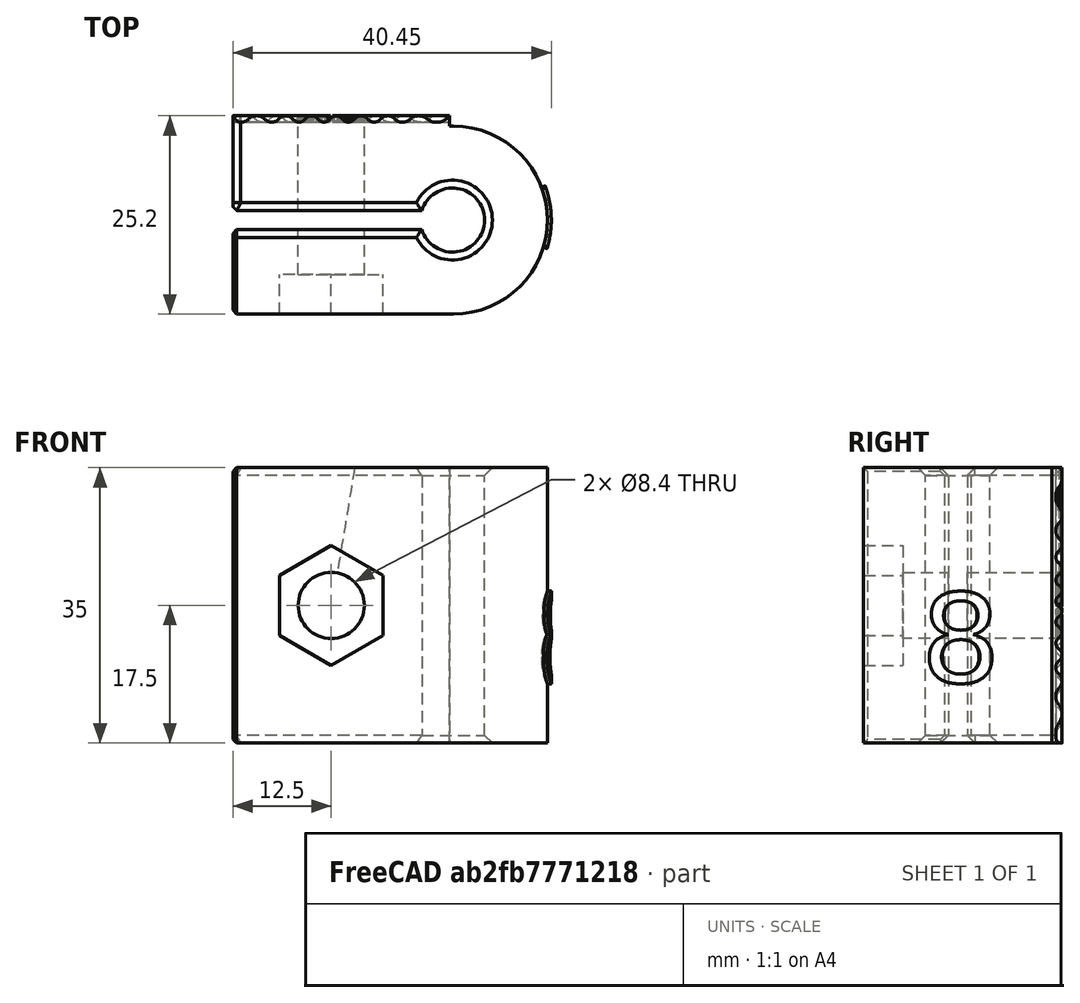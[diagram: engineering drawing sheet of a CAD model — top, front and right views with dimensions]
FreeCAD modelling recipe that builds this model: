
FCSTD DOCUMENT  (FreeCAD 1.1R43012 (Git))
Label: Rod clamp
License: All rights reserved
LicenseURL: https://en.wikipedia.org/wiki/All_rights_reserved
objects: Part::FeaturePython×3, Sketcher::SketchObject×3, App::Point×2, PartDesign::Body×2, Spreadsheet::Sheet×1, Part::RuledSurface×1, Part::Extrusion×1, Part::Box×1, Part::MultiCommon×1, Part::Part2DObjectPython×1, Part::Cylinder×1, PartDesign::Pad×1, PartDesign::FeatureBase×1, Mesh::Feature×1, PartDesign::Pocket×1, Part::MultiFuse×1, Part::Cut×1, Part::Chamfer×1
note: 28 computed .brp shape members not serialized (recipe doc carries the construction recipe); baked Part::Feature solids carry a one-line shape summary decoded from their .brp

FEATURE [Spreadsheet::Sheet] Spreadsheet  label="Parameters"
  cells = A1='Description of parameter; B1='Measurement; A2='Bolt diameter (mm); B2(bolt)=8; A3='Bolt diameter tolerance (mm); B3(BoltTolerance)=0.4; A4='Rod diameter (mm); B4(rod)=8; A5='Rod diameter tolerance (mm); B5(RodTolerance)=0.15; A7='Interface parameters; A8='Inner radius; B8(InnerRadius)=2; A9='Outer radius; B9(OuterRadius)=25; A10='Amplitude of waves; B10(amplitude)=0.8; A11='Number of waves; B11(NumberOfWaves)=36; A12='Interval (do not change); B12(Interval)=0.01
FEATURE [Part::FeaturePython] ParametricCurve  # WARN: FeaturePython — macro-defined, semantics opaque (R4)
  AttacherType = Attacher::AttachEngine3D
  Closed = false
  Continuity = C2
  EditFormulas = false
  F_X = 0
  F_Y = 0
  F_Z = 0
  F_a = 25
  F_b = 36
  F_c = 0.8
  F_d = [0,0]
  FormulaName = formula1
  Formulas = 0
  Interval = 0.01
  MakeFace = false
  PlusOneIteration = true
  Points = (630) [(25,0,0.4),(24.9988,0.249996,0.602621),(24.995,0.499967,0.738292),(24.9888,0.749888,0.791969),(24.98,0.999733,0.799956),(24.9688,1.24948,0.799593),+624 more]
  ShapeType = 0
  Sorted = false
  UpdateSpreadsheet = false
  UseSpreadsheet = false
  Version = 2023.05.06
  X = a*cos(t)
  Y = a*sin(t)
  Z = c * ( 3*((1 + sin(b*t))/2)^2 - 2*((1 + sin(b*t))/2)^3 )
  a = 25
  b = 36
  c = 0.8
  t_max = 6.28319
  t_min = 0
  expr: Interval = .Spreadsheet.Interval
  expr: a = .Spreadsheet.OuterRadius
  expr: b = .Spreadsheet.NumberOfWaves
  expr: c = .Spreadsheet.amplitude
FEATURE [Part::FeaturePython] ParametricCurve001  # WARN: FeaturePython — macro-defined, semantics opaque (R4)
  AttacherType = Attacher::AttachEngine3D
  Closed = false
  Continuity = C2
  EditFormulas = false
  F_X = 0
  F_Y = 0
  F_Z = 0
  F_a = 2
  F_b = 36
  F_c = 0.8
  F_d = [0,0]
  FormulaName = formula2
  Formulas = 0
  Interval = 0.01
  MakeFace = false
  PlusOneIteration = true
  Points = (630) [(2,0,0.4),(1.9999,0.0199997,0.602621),(1.9996,0.0399973,0.738292),(1.9991,0.059991,0.791969),(1.9984,0.0799787,0.799956),(1.9975,0.0999583,0.799593),+624 more]
  ShapeType = 0
  Sorted = false
  UpdateSpreadsheet = false
  UseSpreadsheet = false
  Version = 2023.05.06
  X = a*cos(t)
  Y = a*sin(t)
  Z = c * ( 3*((1 + sin(b*t))/2)^2 - 2*((1 + sin(b*t))/2)^3 )
  a = 2
  b = 36
  c = 0.8
  t_max = 6.28319
  t_min = 0
  expr: Interval = .Spreadsheet.Interval
  expr: a = .Spreadsheet.InnerRadius
  expr: b = .Spreadsheet.NumberOfWaves
  expr: c = .Spreadsheet.amplitude
FEATURE [Part::RuledSurface] Ruled_Surface
  Curve1 = -> ParametricCurve [Edge1]
  Curve2 = -> ParametricCurve001 [Edge1]
  Orientation = 0
  Placement = pos=(10,-3.75,-17.5) rot=(0.020938,0.999562,0.020938;1.57123rad)
FEATURE [Part::Extrusion] Extrude003
  Base = -> Ruled_Surface
  Dir = (-1,0,0)
  DirMode = 0
  FaceMakerClass = Part::FaceMakerBullseye
  FaceMakerMode = 3
  LengthFwd = 2
  LengthRev = 0
  Placement = pos=(7e-15,-0.879345,0.597287) rot=(1,0,0;0.122173rad)
  Solid = false
  Symmetric = false
FEATURE [Part::Box] Box  label="Cube"
  AttacherType = Attacher::AttachEngine3D
  Height = 1.5
  Length = 35
  Placement = pos=(9.4513,-15,0) rot=(0,1,0;1.5708rad)
  Width = 27.5
FEATURE [Part::MultiCommon] Common
  Placement = pos=(0,0,0) rot=(0,1,0;3.14159rad)
  Shapes = -> [Box,Extrude003]
FEATURE [Part::Part2DObjectPython] ShapeString  # Draft 2D object (typed FeaturePython)
  FontFile = <path>
  Fuse = false
  Justification = 4
  JustificationReference = 0
  KeepLeftMargin = false
  MakeFace = true
  ObliqueAngle = 0
  Placement = pos=(30,4.85425,0) rot=(0,0,1;0rad)
  ScaleToSize = true
  Size = 16
  String = 8
  Tracking = 0
FEATURE [Part::Cylinder] Cylinder
  Angle = 360
  AttacherType = Attacher::AttachEngine3D
  FirstAngle = 0
  Height = 30
  Placement = pos=(-15,-2.5,-17.5) rot=(0,1,0;1.5708rad)
  Radius = 4.2
  SecondAngle = 0
  expr: Radius = (Spreadsheet.bolt + Spreadsheet.BoltTolerance) / 2
FEATURE [Sketcher::SketchObject] Sketch
  ArcFitTolerance = 1e-06
  AttachmentSupport = -> [Origin]
  ExternalTypes = [0]
  FullyConstrained = true
  MakeInternals = false
  MapMode = 5
  expr: Constraints[16] = (Spreadsheet.rod + Spreadsheet.RodTolerance) / 2
  sketch-geometry (8):
    g0: LineSegment StartX=-11.95 StartY=-15 StartZ=0 EndX=-11.95 EndY=13 EndZ=0
    g1: LineSegment StartX=-11.95 StartY=-15 StartZ=0 EndX=-1.2 EndY=-15 EndZ=0
    g2: LineSegment StartX=-1.2 StartY=-15 StartZ=0 EndX=-1.2 EndY=9 EndZ=0
    g3: LineSegment StartX=1.2 StartY=9 StartZ=0 EndX=1.2 EndY=-15 EndZ=0
    g4: LineSegment StartX=1.2 StartY=-15 StartZ=0 EndX=11.95 EndY=-15 EndZ=0
    g5: LineSegment StartX=11.95 StartY=-15 StartZ=0 EndX=11.95 EndY=13 EndZ=0
    g6: ArcOfCircle CenterX=-3e-16 CenterY=13 CenterZ=0 NormalX=0 NormalY=0 NormalZ=1 AngleXU=0 Radius=11.95 StartAngle=6.28319 EndAngle=9.42478
    g7: ArcOfCircle CenterX=-2.2e-15 CenterY=12.8943 CenterZ=0 NormalX=0 NormalY=0 NormalZ=1 AngleXU=0 Radius=4.075 StartAngle=5.0113 EndAngle=10.6967
  constraints (26):
    c: Vertical(g0)
    c: Coincident(g0,g1)
    c: Horizontal(g1)
    c: Coincident(g1,g2)
    c: Vertical(g3)
    c: Coincident(g3,g4)
    c: Horizontal(g4)
    c: Coincident(g4,g5)
    c: Vertical(g5)
    c: Coincident(g0,g6)
    c: Coincident(g6,g5)
    c: DistanceY(g3,g-1) = 15
    c: DistanceY(g1,g-1) = 15
    c: Coincident(g3,g7)
    c: Vertical(g2)
    c: Coincident(g7,g2)
    c: Radius(g7) = 4.075
    c: DistanceY(g2,g3) = 0
    c: DistanceY(g3,g3) = 24
    c: DistanceY(g5,g0) = 0
    c: DistanceY(g4,g5) = 28
    c: DistanceX(g4,g4) = 10.75
    c: Equal(g1,g4)
    c: Distance(g1,g-2) = 1.2
    c: Distance(g3,g-2) = 1.2
    c: Radius(g6) = 11.95
FEATURE [PartDesign::Pad] Pad
  Direction = (0,0,1)
  Length = 35
  Length2 = 10
  Profile = -> Sketch
  ReferenceAxis = -> Sketch [N_Axis]
  Refine = true
  Reversed = true
  Suppressed = false
  Type = 0
FEATURE [Sketcher::SketchObject] Mapped_Sketch
  ArcFitTolerance = 1e-06
  AttachmentSupport = -> [Pad]
  ExternalTypes = [0]
  FullyConstrained = false
  MakeInternals = false
  Placement = pos=(3.03142,5.20342,0) rot=(0,0,1;0rad)
  sketch-geometry (8):
    g0: LineSegment [constr] StartX=0 StartY=0 StartZ=0 EndX=27.0812 EndY=0 EndZ=0
    g1: LineSegment [constr] StartX=27.0812 StartY=0 StartZ=0 EndX=27.0812 EndY=30 EndZ=0
    g2: LineSegment [constr] StartX=27.0812 StartY=30 StartZ=0 EndX=0 EndY=30 EndZ=0
    g3: LineSegment [constr] StartX=0 StartY=30 StartZ=0 EndX=0 EndY=0 EndZ=0
    g4: LineSegment [constr] StartX=10.2789 StartY=6.24604 StartZ=0 EndX=10.2789 EndY=-19.2688 EndZ=0
    g5: LineSegment [constr] StartX=10.2789 StartY=-19.2688 StartZ=0 EndX=52.8869 EndY=-19.2688 EndZ=0
    g6: LineSegment [constr] StartX=52.8869 StartY=-19.2688 StartZ=0 EndX=52.8869 EndY=6.24604 EndZ=0
    g7: LineSegment [constr] StartX=52.8869 StartY=6.24604 StartZ=0 EndX=10.2789 EndY=6.24604 EndZ=0
  constraints (19):
    c: Coincident(g0,g-1)
    c: Coincident(g0,g1)
    c: Coincident(g1,g2)
    c: Coincident(g2,g3)
    c: Coincident(g3,g0)
    c: Horizontal(g0)
    c: Horizontal(g2)
    c: Vertical(g1)
    c: Vertical(g3)
    c: DistanceX(g2,g2) = 27.0812
    c: DistanceY(g1,g1) = 30
    c: Coincident(g4,g5)
    c: Coincident(g5,g6)
    c: Coincident(g6,g7)
    c: Coincident(g7,g4)
    c: Vertical(g4)
    c: Vertical(g6)
    c: Horizontal(g5)
    c: Horizontal(g7)
FEATURE [App::Point] Origin001
  Role = Origin
FEATURE [Part::FeaturePython] Sketch_On_Surface  # WARN: FeaturePython — macro-defined, semantics opaque (R4)
  ConstructionBounds = true
  ExtraObjects = -> [ShapeString]
  FillExtrusion = true
  FillFaces = true
  ReverseU = false
  ReverseV = false
  Sketch = -> Mapped_Sketch
  SwapUV = false
  Thickness = 0.5
FEATURE [PartDesign::FeatureBase] Clone001
  BaseFeature = -> Common
  Placement = pos=(0.0566779,0,-30) rot=(0,0,0;3.14159rad)
  Suppressed = false
FEATURE [App::Point] Origin005
  Role = Origin
FEATURE [PartDesign::Body] Body002  label="Interface 2"
  AllowCompound = false
  Group = -> [Clone001]
  Origin = -> Origin004
  Placement = pos=(-2.5,3.47e-14,-5) rot=(0,0,1;0rad)
  Tip = -> Clone001
FEATURE [Mesh::Feature] RODCLAMP_8MM
  Placement = pos=(0,13,-17.5) rot=(0,0,-1;1.5708rad)
FEATURE [Sketcher::SketchObject] Sketch001
  ArcFitTolerance = 1e-06
  AttachmentSupport = -> [Pad]
  ExternalTypes = [0]
  FullyConstrained = true
  MakeInternals = false
  MapMode = 5
  Placement = pos=(11.95,0,0) rot=(0.57735,0.57735,0.57735;2.0944rad)
  sketch-geometry (7):
    g0: LineSegment StartX=-2.5 StartY=-9.9 StartZ=0 EndX=-9.08179 EndY=-13.7 EndZ=0
    g1: LineSegment StartX=-9.08179 StartY=-13.7 StartZ=0 EndX=-9.08179 EndY=-21.3 EndZ=0
    g2: LineSegment StartX=-9.08179 StartY=-21.3 StartZ=0 EndX=-2.5 EndY=-25.1 EndZ=0
    g3: LineSegment StartX=-2.5 StartY=-25.1 StartZ=0 EndX=4.08179 EndY=-21.3 EndZ=0
    g4: LineSegment StartX=4.08179 StartY=-21.3 StartZ=0 EndX=4.08179 EndY=-13.7 EndZ=0
    g5: LineSegment StartX=4.08179 StartY=-13.7 StartZ=0 EndX=-2.5 EndY=-9.9 EndZ=0
    g6: Circle [constr] CenterX=-2.5 CenterY=-17.5 CenterZ=0 NormalX=0 NormalY=0 NormalZ=1 AngleXU=0 Radius=7.6
  constraints (17):
    c: Coincident(g0,g1)
    c: Coincident(g1,g2)
    c: Coincident(g2,g3)
    c: Coincident(g3,g4)
    c: Coincident(g4,g5)
    c: Coincident(g5,g0)
    c: Equal(g0, g1-g5) x5
    c: PointOnObject(g0,g6)
    c: PointOnObject(g1,g6)
    c: PointOnObject(g2,g6)
    c: PointOnObject(g3,g6)
    c: PointOnObject(g4,g6)
    c: PointOnObject(g5,g6)
    c: Distance(g0,g-2) = 2.5
    c: Distance(g2,g-2) = 2.5
    c: DistanceY(g6,g-1) = 17.5
    c: DistanceY(g2,g0) = 15.2
FEATURE [PartDesign::Pocket] Pocket
  BaseFeature = -> Pad
  Direction = (-1,0,0)
  Length = 5
  Length2 = 5
  Profile = -> Sketch001
  ReferenceAxis = -> Sketch001 [N_Axis]
  Refine = true
  Suppressed = false
  Type = 0
FEATURE [PartDesign::Body] Body  label="Main clamp body"
  AllowCompound = false
  Group = -> [Sketch,Pad,Sketch001,Pocket]
  Origin = -> Origin
  Tip = -> Pocket
FEATURE [Part::MultiFuse] Fusion
  Shapes = -> [Body,Sketch_On_Surface,Body002]
FEATURE [Part::Cut] Cut
  Base = -> Fusion
  Tool = -> Cylinder
FEATURE [Part::Chamfer] Chamfer
  Base = -> Cut
  EdgeLinks = -> Cut [Edge3,Edge4,Edge5,Edge6,Edge7,Edge9,Edge10,Edge11,Edge13,Edge19,Edge20,Edge26,Edge27]
  Edges = 13 edges: [Edge3 r=1,Edge4 r=1,Edge5 r=1,Edge6 r=1,Edge7 r=0.5,Edge9 r=0.5,Edge10 r=1,Edge11 r=1,Edge13 r=1,Edge19 r=0.5,Edge20 r=1,Edge26 r=0.5,Edge27 r=0.5]
  Placement = pos=(0,0,0) rot=(0,0,1;4.71239rad)
note: 1 file-system path scrubbed to <path> (originals preserved in the JSON sidecar)
